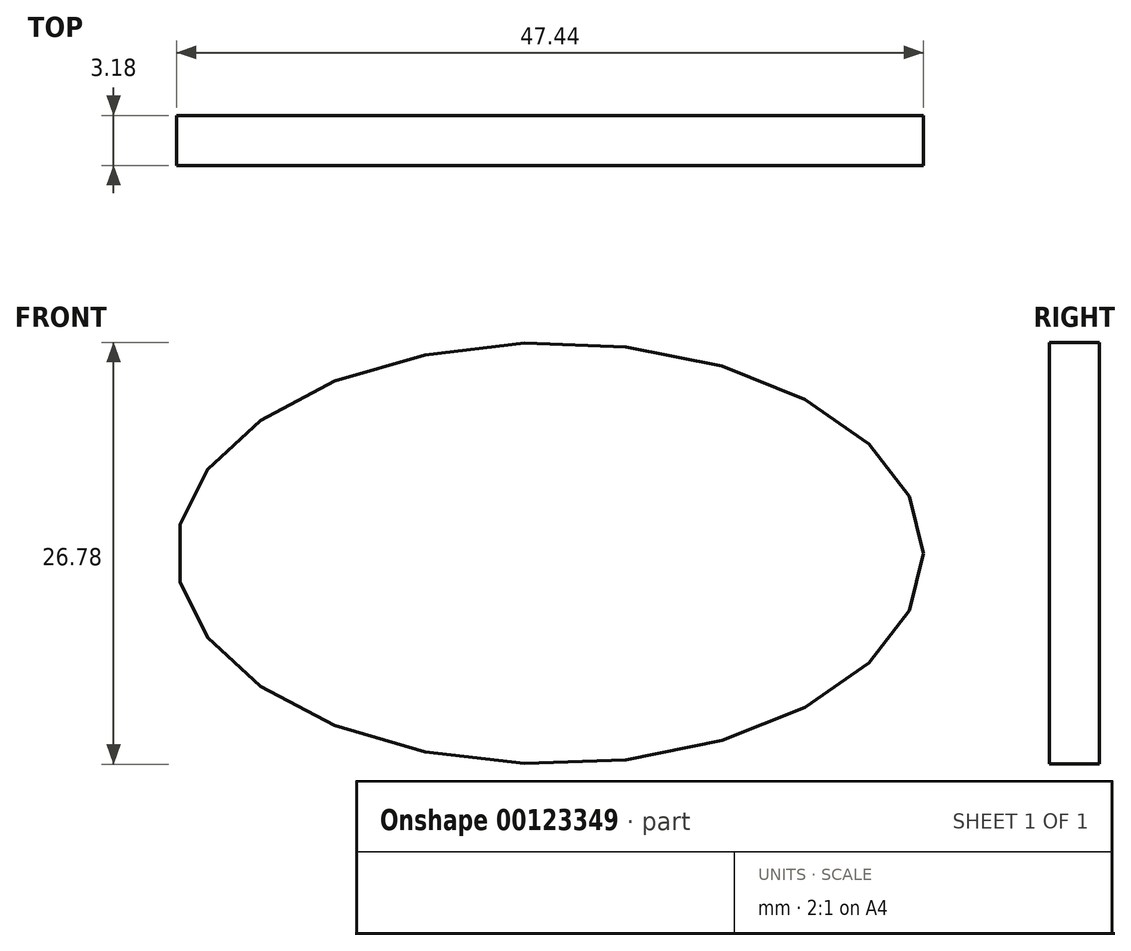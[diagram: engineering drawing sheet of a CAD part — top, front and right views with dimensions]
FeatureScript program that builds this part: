
annotation { "Feature Type Name" : "Feature", "Feature Type Description" : "" }
export const myFeature = defineFeature(function(context is Context, id is Id, definition is map)
    precondition{}
    {
        {
            var Q0;
            Q0=qCreatedBy(makeId("Front.planeOp"),FACE);
            var sketch = newSketch(context, id + "F0", { "sketchPlane" : qUnion([Q0])});
            skEllipse(sketch, "E0", {"center": v(0, 57.15) * mm, "majorRadius": 23.72 * mm, "minorRadius": 13.39 * mm, "majorAxis": v(1, 0)});
            skLineSegment(sketch, "E1.right", {"start": v(37.83, 58.04) * mm, "end": v(37.83, 58.39) * mm});
            skSolve(sketch);
        }
        {
            var Q0;
            {var subQ0=sQuery(id+"F0.wireOp",EDGE,"1d2c4bc0-d696-45fc-aee5-ab138a4aa73d");Q0=makeQuery(id+"F0.imprint","IMPRINT",FACE,{"disambiguationData":[TD([[makeQuery(id+"F0.imprint","IMPRINT",EDGE,{"derivedFrom":subQ0}),1.0]])]});}
            var Q1;
            Q1=makeQuery(id+"F0.imprint","IMPRINT",FACE,{"disambiguationData":[TD([[makeQuery(id+"F0.imprint","IMPRINT",EDGE,{"derivedFrom":sQuery(id+"F0.wireOp",EDGE,"E0")}),-1.0]])]});
            var Q2;
            {var subQ1=sQuery(id+"F0.wireOp",EDGE,"Rg2uVKMv-AShf-P7mx-oSHO-kPYZmrgVDCv9");Q2=makeQuery(id+"F0.imprint","IMPRINT",FACE,{"disambiguationData":[TD([[makeQuery(id+"F0.imprint","IMPRINT",EDGE,{"derivedFrom":subQ1}),1.0]])]});}
            var Q3;
            Q3=makeQuery(id+"F0.imprint","IMPRINT",FACE,{"disambiguationData":[TD([[makeQuery(id+"F0.imprint","IMPRINT",EDGE,{"derivedFrom":sQuery(id+"F0.wireOp",EDGE,"069306ae-f67a-4aa1-aade-24fc15e266e9.bottom")}),-1.0]])]});
            var Q4;
            {var subQ0=sQuery(id+"F0.wireOp",EDGE,"eb30e788-97d2-4e6d-9a34-bc0e9ed86b70");Q4=makeQuery(id+"F0.imprint","IMPRINT",FACE,{"disambiguationData":[TD([[makeQuery(id+"F0.imprint","IMPRINT",EDGE,{"derivedFrom":subQ0}),1.0]])]});}
            var Q5;
            Q5=makeQuery(id+"F0.imprint","IMPRINT",FACE,{"disambiguationData":[TD([[makeQuery(id+"F0.imprint","IMPRINT",EDGE,{"derivedFrom":sQuery(id+"F0.wireOp",EDGE,"E0")}),1.0]])]});
            var Q6;
            {var subQ4=sQuery(id+"F0.wireOp",EDGE,"E1.top");Q6=makeQuery(id+"F0.imprint","IMPRINT",FACE,{"disambiguationData":[TD([[makeQuery(id+"F0.imprint","IMPRINT",EDGE,{"derivedFrom":subQ4}),-1.0]])]});}
            var Q7;
            Q7=makeQuery(id+"F0.imprint","IMPRINT",FACE,{"disambiguationData":[TD([[makeQuery(id+"F0.imprint","IMPRINT",EDGE,{"derivedFrom":sQuery(id+"F0.wireOp",EDGE,"8aaf0393-9328-45a1-8438-03d08ab25ff1.bottom")}),1.0]])]});
            var Q8;
            {var subQ0=sQuery(id+"F0.wireOp",EDGE,"SHurT9tC-O9KN-FOhH-H2UF-MryJ8sBad2kW");Q8=makeQuery(id+"F0.imprint","IMPRINT",FACE,{"disambiguationData":[TD([[makeQuery(id+"F0.imprint","IMPRINT",EDGE,{"derivedFrom":subQ0}),-1.0]])]});}
            var Q9;
            {var subQ0=sQuery(id+"F0.wireOp",EDGE,"KfIL0Aif-151c-r6aj-pm4L-LaXWSolLJvXY");Q9=makeQuery(id+"F0.imprint","IMPRINT",FACE,{"disambiguationData":[TD([[makeQuery(id+"F0.imprint","IMPRINT",EDGE,{"derivedFrom":subQ0}),1.0]])]});}
            extrude(context, id + "F1", {"entities" : qUnion([Q0, Q1, Q2, Q3, Q4, Q5, Q6, Q7, Q8, Q9]), "oppositeDirection" : true, "depth" : 3.17 * mm});
        }
    });
